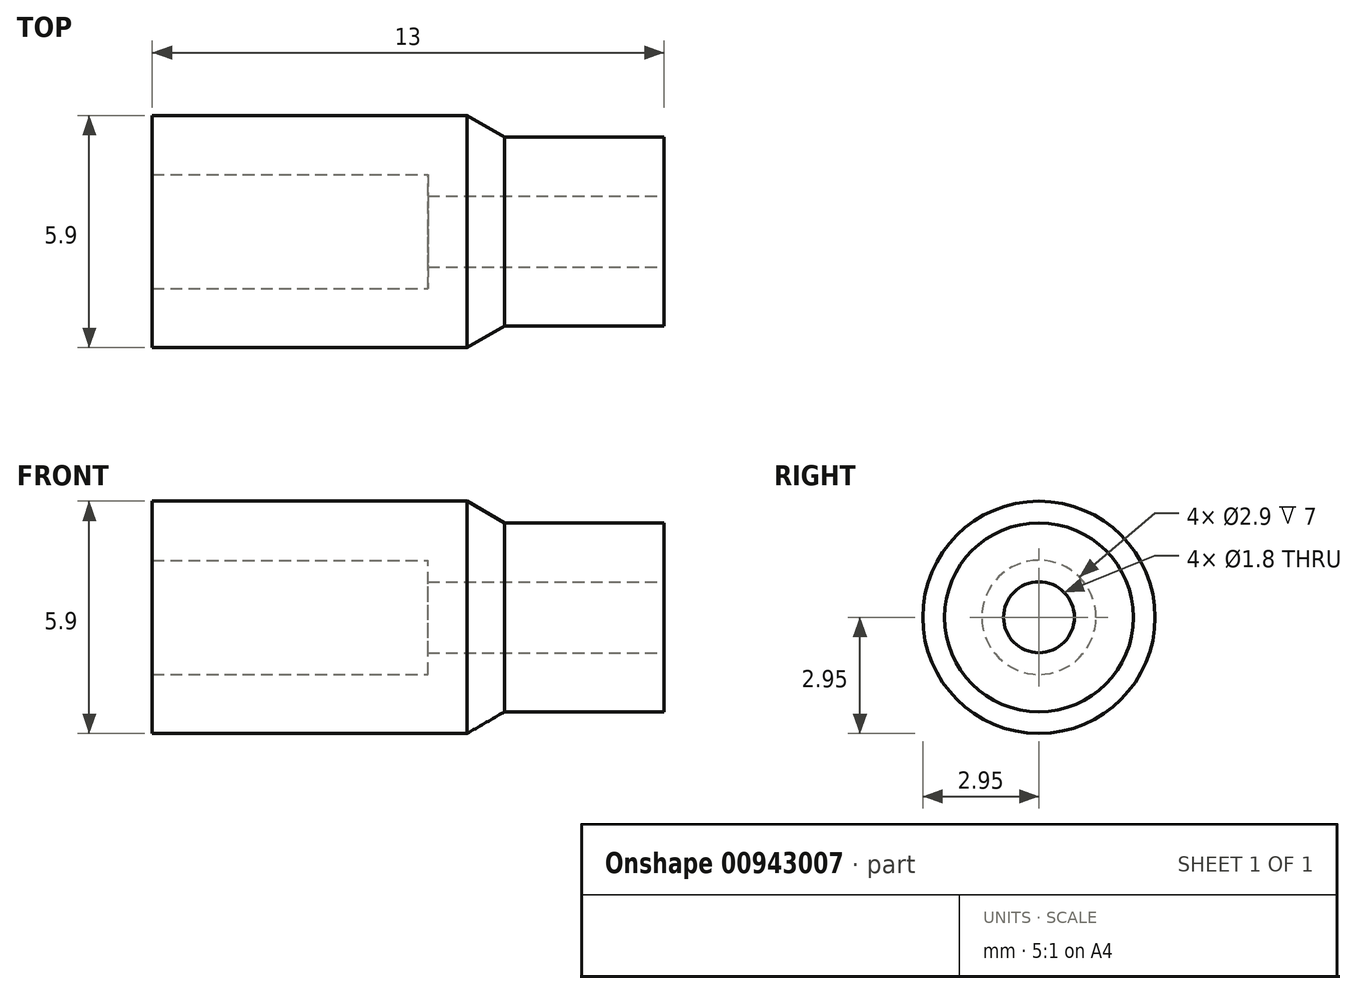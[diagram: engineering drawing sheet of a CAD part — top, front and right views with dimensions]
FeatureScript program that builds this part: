
annotation { "Feature Type Name" : "Feature", "Feature Type Description" : "" }
export const myFeature = defineFeature(function(context is Context, id is Id, definition is map)
    precondition{}
    {
        {
            var Q0;
            Q0=qCreatedBy(makeId("Front.planeOp"),FACE);
            var sketch = newSketch(context, id + "F0", { "sketchPlane" : qUnion([Q0])});
            skLineSegment(sketch, "E0", {"start": v(-7, 1.45) * mm, "end": v(-7, 2.95) * mm});
            skLineSegment(sketch, "E1", {"start": v(-7, 2.95) * mm, "end": v(1, 2.95) * mm});
            skLineSegment(sketch, "E2", {"start": v(1, 2.95) * mm, "end": v(1, 2.4) * mm});
            skLineSegment(sketch, "E3", {"start": v(1, 2.4) * mm, "end": v(6, 2.4) * mm});
            skLineSegment(sketch, "E4", {"start": v(6, 2.4) * mm, "end": v(6, 0.9) * mm});
            skLineSegment(sketch, "E5", {"start": v(3.33, 0) * mm, "end": v(-3.47, 0) * mm, "construction": true});
            skLineSegment(sketch, "E6", {"start": v(-7, 1.45) * mm, "end": v(0, 1.45) * mm});
            skLineSegment(sketch, "E7", {"start": v(0, 1.45) * mm, "end": v(0, 0.9) * mm});
            skLineSegment(sketch, "E8", {"start": v(0, 0.9) * mm, "end": v(6, 0.9) * mm});
            skLineSegment(sketch, "E9", {"start": v(1, 2.95) * mm, "end": v(1.95, 2.4) * mm});
            skSolve(sketch);
        }
        {
            var Q0;
            Q0 = qSketchRegion(id + "F0", true);
            var Q1;
            Q1=sQuery(id+"F0.wireOp",EDGE,"E5");
            revolve(context, id + "F1", {"surfaceOperationType" : NewSurfaceOperationType.NEW, "entities" : qUnion([Q0]), "axis" : qUnion([Q1]), "revolveType" : RevolveType.FULL});
        }
    });
